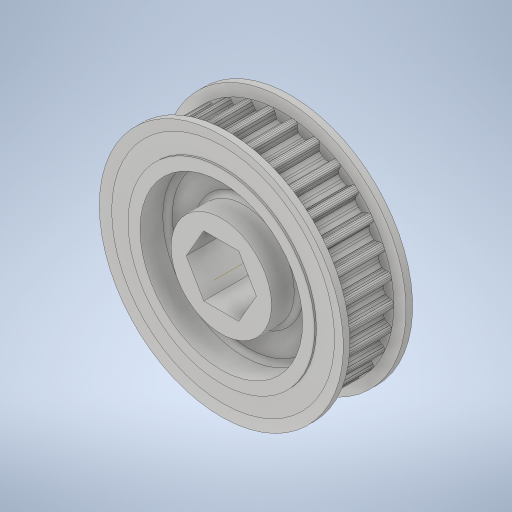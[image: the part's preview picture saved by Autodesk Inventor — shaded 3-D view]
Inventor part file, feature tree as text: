
AUTODESK INVENTOR PART (.ipt)
format: ipt  version: 2023.3 (Build 273359000, 359)  size: 1,093,632 bytes
history: native  units: in
note: dims shown in document units (in); Inventor stores cm internally (conversion verified against a paired STEP export)
features: mirror x1
ambient origin geometry x8: Origin, YZ Plane, XZ Plane, XY Plane, X Axis, Y Axis, Z Axis, Center Point
bodies: Solid1 (feature_tree)
feature tree (1):
  mirror  "Mirror1"
